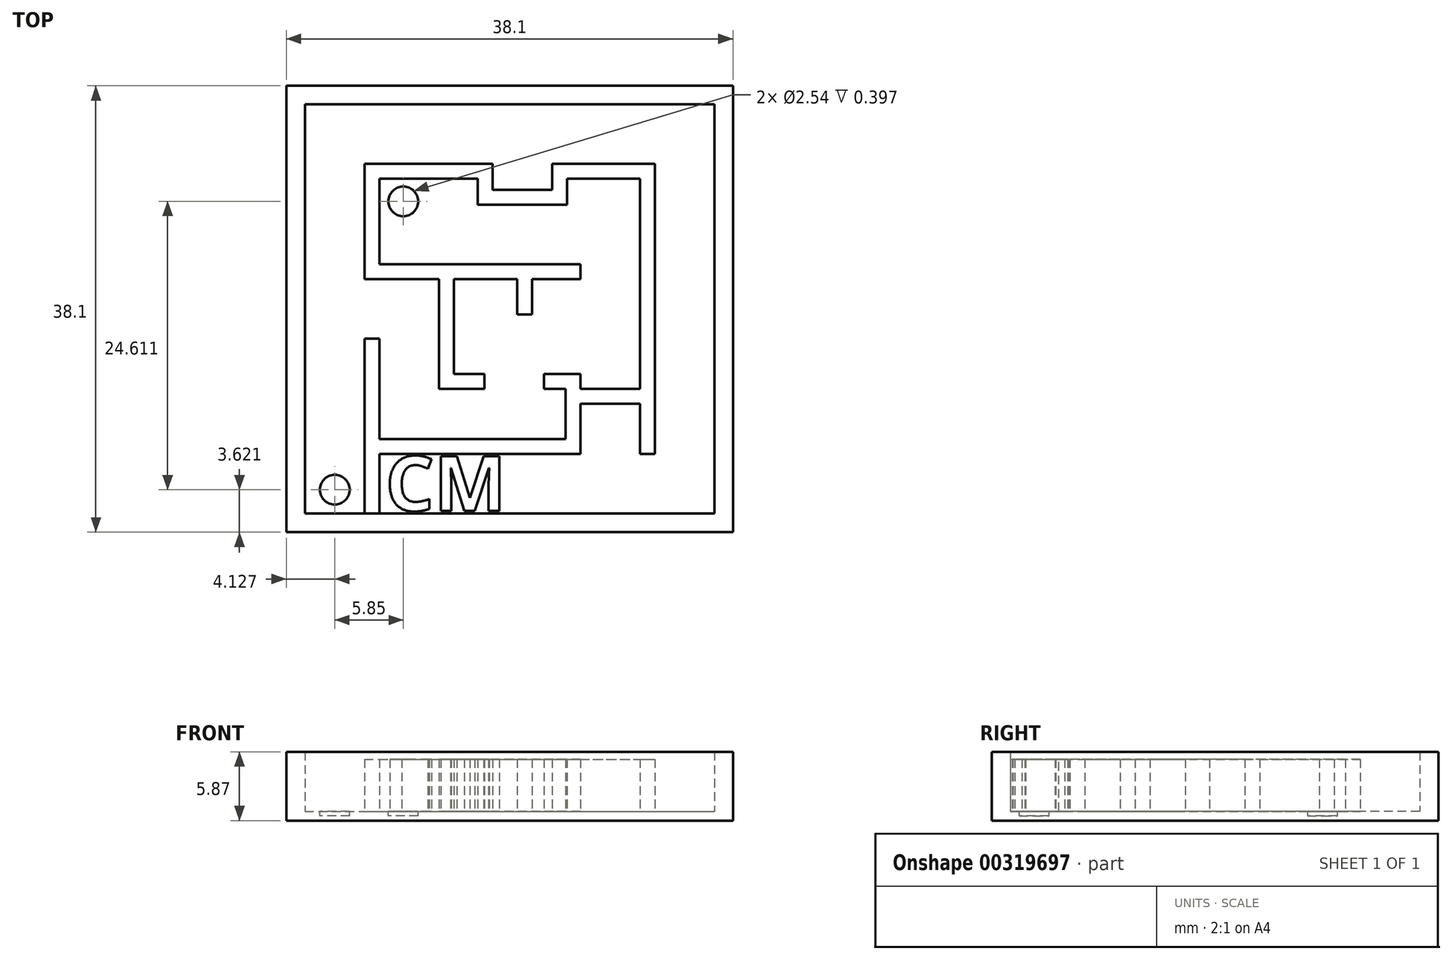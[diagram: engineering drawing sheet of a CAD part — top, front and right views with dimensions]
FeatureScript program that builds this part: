
annotation { "Feature Type Name" : "Feature", "Feature Type Description" : "" }
export const myFeature = defineFeature(function(context is Context, id is Id, definition is map)
    precondition{}
    {
        {
            var Q0;
            Q0=qCreatedBy(makeId("Top.planeOp"),FACE);
            var sketch = newSketch(context, id + "F0", { "sketchPlane" : qUnion([Q0])});
            skLineSegment(sketch, "E0.bottom", {"start": v(-16.34, 17.08) * mm, "end": v(21.76, 17.08) * mm});
            skLineSegment(sketch, "E0.top", {"start": v(-16.34, -21.02) * mm, "end": v(21.76, -21.02) * mm});
            skLineSegment(sketch, "E0.left", {"start": v(-16.34, 17.08) * mm, "end": v(-16.34, -21.02) * mm});
            skLineSegment(sketch, "E0.right", {"start": v(21.76, 17.08) * mm, "end": v(21.76, -21.02) * mm});
            skSolve(sketch);
        }
        {
            var Q0;
            Q0=makeQuery(id+"F0.imprint","IMPRINT",FACE,{"disambiguationData":[TD([[makeQuery(id+"F0.imprint","IMPRINT",EDGE,{"derivedFrom":sQuery(id+"F0.wireOp",EDGE,"E0.bottom")}),-1.0]])]});
            extrude(context, id + "F1", {"entities" : qUnion([Q0]), "depth" : 0.8 * mm});
        }
        {
            var Q0;
            Q0=makeQuery(id+"F1.opExtrude","CAP_FACE",FACE,{"disambiguationData":[OSD([sQuery(id+"F0.wireOp",EDGE,"E0.bottom"),sQuery(id+"F0.wireOp",EDGE,"E0.top"),sQuery(id+"F0.wireOp",EDGE,"E0.left"),sQuery(id+"F0.wireOp",EDGE,"E0.right")])],"isStart":false});
            var sketch = newSketch(context, id + "F2", { "sketchPlane" : qUnion([Q0])});
            skLineSegment(sketch, "E1.0", {"start": v(-14.75, 15.5) * mm, "end": v(20.17, 15.5) * mm});
            skLineSegment(sketch, "E1.1", {"start": v(-14.75, 15.5) * mm, "end": v(-14.75, -19.43) * mm});
            skLineSegment(sketch, "E1.2", {"start": v(-14.75, -19.43) * mm, "end": v(20.17, -19.43) * mm});
            skLineSegment(sketch, "E1.3", {"start": v(20.17, 15.5) * mm, "end": v(20.17, -19.43) * mm});
            skSolve(sketch);
        }
        {
            var Q0;
            Q0=makeQuery(id+"F2.imprint","IMPRINT",FACE,{"disambiguationData":[TD([[makeQuery(id+"F2.imprint","IMPRINT",EDGE,{"derivedFrom":sQuery(id+"F2.wireOp",EDGE,"E1.0")}),1.0]])]});
            extrude(context, id + "F3", {"entities" : qUnion([Q0]), "operationType" : NewBodyOperationType.ADD, "depth" : 5.08 * mm});
        }
        {
            var Q0;
            Q0=makeQuery(id+"F1.opExtrude","CAP_FACE",FACE,{"disambiguationData":[OSD([sQuery(id+"F0.wireOp",EDGE,"E0.bottom"),sQuery(id+"F0.wireOp",EDGE,"E0.top"),sQuery(id+"F0.wireOp",EDGE,"E0.left"),sQuery(id+"F0.wireOp",EDGE,"E0.right")])],"isStart":false});
            var sketch = newSketch(context, id + "F4", { "sketchPlane" : qUnion([Q0])});
            skLineSegment(sketch, "E2.bottom", {"start": v(-9.67, -19.43) * mm, "end": v(-8.4, -19.43) * mm});
            skLineSegment(sketch, "E2.top", {"start": v(-9.67, 10.41) * mm, "end": v(-8.4, 10.41) * mm});
            skLineSegment(sketch, "E2.left", {"start": v(-9.67, -19.43) * mm, "end": v(-9.67, -4.5) * mm});
            skLineSegment(sketch, "E2.right", {"start": v(-8.4, -19.43) * mm, "end": v(-8.4, -4.5) * mm});
            skLineSegment(sketch, "E3", {"start": v(-9.67, 0.57) * mm, "end": v(-8.4, 0.57) * mm});
            skLineSegment(sketch, "E4", {"start": v(-9.67, -4.5) * mm, "end": v(-8.4, -4.5) * mm});
            skLineSegment(sketch, "E5.trimOffspring", {"start": v(-9.67, 0.57) * mm, "end": v(-9.67, 10.41) * mm});
            skLineSegment(sketch, "E6.trimOffspring", {"start": v(-8.4, 0.57) * mm, "end": v(-8.4, 10.41) * mm});
            skLineSegment(sketch, "E7.bottom", {"start": v(-8.4, 10.41) * mm, "end": v(1.27, 10.41) * mm});
            skLineSegment(sketch, "E7.top", {"start": v(-8.4, 9.14) * mm, "end": v(1.27, 9.14) * mm});
            skLineSegment(sketch, "E7.left", {"start": v(-8.4, 10.41) * mm, "end": v(-8.4, 9.14) * mm});
            skLineSegment(sketch, "E7.right", {"start": v(15.1, 10.41) * mm, "end": v(15.1, 9.14) * mm});
            skLineSegment(sketch, "E8.bottom", {"start": v(15.1, 9.14) * mm, "end": v(13.82, 9.14) * mm});
            skLineSegment(sketch, "E8.top", {"start": v(15.1, 4.7) * mm, "end": v(13.82, 4.7) * mm});
            skLineSegment(sketch, "E8.left", {"start": v(15.1, 9.14) * mm, "end": v(15.1, 4.7) * mm});
            skLineSegment(sketch, "E8.right", {"start": v(13.82, 9.14) * mm, "end": v(13.82, 4.7) * mm});
            skLineSegment(sketch, "E9.bottom", {"start": v(-8.4, 0.57) * mm, "end": v(-2.05, 0.57) * mm});
            skLineSegment(sketch, "E9.top", {"start": v(-8.4, 1.84) * mm, "end": v(-2.05, 1.84) * mm});
            skLineSegment(sketch, "E9.left", {"start": v(-8.4, 0.57) * mm, "end": v(-8.4, 1.84) * mm});
            skLineSegment(sketch, "E9.right", {"start": v(-2.05, 0.57) * mm, "end": v(-2.05, 1.84) * mm});
            skLineSegment(sketch, "E10.bottom", {"start": v(-2.05, 0.57) * mm, "end": v(-3.32, 0.57) * mm});
            skLineSegment(sketch, "E10.top", {"start": v(-2.05, -8) * mm, "end": v(-3.32, -8) * mm});
            skLineSegment(sketch, "E10.left", {"start": v(-2.05, 0.57) * mm, "end": v(-2.05, -8) * mm});
            skLineSegment(sketch, "E10.right", {"start": v(-3.32, 0.57) * mm, "end": v(-3.32, -8) * mm});
            skPoint(sketch, "E11.oppositeSnap0", {"position": v(13.82, 6.92) * mm});
            skLineSegment(sketch, "E11.bottom", {"start": v(-3.32, 9.14) * mm, "end": v(-2.05, 9.14) * mm});
            skLineSegment(sketch, "E12.bottom", {"start": v(13.82, 4.7) * mm, "end": v(15.1, 4.7) * mm});
            skLineSegment(sketch, "E12.top", {"start": v(13.82, -8) * mm, "end": v(15.1, -8) * mm});
            skLineSegment(sketch, "E12.left", {"start": v(13.82, 4.7) * mm, "end": v(13.82, -8) * mm});
            skLineSegment(sketch, "E12.right", {"start": v(15.1, 4.7) * mm, "end": v(15.1, -8) * mm});
            skLineSegment(sketch, "E13.bottom", {"start": v(-2.05, 0.57) * mm, "end": v(8.74, 0.57) * mm});
            skLineSegment(sketch, "E13.top", {"start": v(-2.05, 1.84) * mm, "end": v(8.74, 1.84) * mm});
            skLineSegment(sketch, "E13.right", {"start": v(8.74, 0.57) * mm, "end": v(8.74, 1.84) * mm});
            skLineSegment(sketch, "E14.bottom", {"start": v(-0.71, 1.84) * mm, "end": v(0.56, 1.84) * mm});
            skLineSegment(sketch, "E15.bottom", {"start": v(11.44, 9.14) * mm, "end": v(10.17, 9.14) * mm});
            skLineSegment(sketch, "E16.bottom", {"start": v(-8.4, -13.08) * mm, "end": v(8.74, -13.08) * mm});
            skLineSegment(sketch, "E16.top", {"start": v(-8.4, -14.35) * mm, "end": v(8.74, -14.35) * mm});
            skLineSegment(sketch, "E16.left", {"start": v(-8.4, -13.08) * mm, "end": v(-8.4, -14.35) * mm});
            skLineSegment(sketch, "E16.right", {"start": v(8.74, -13.08) * mm, "end": v(8.74, -14.35) * mm});
            skLineSegment(sketch, "E17.top", {"start": v(13.82, -14.35) * mm, "end": v(15.1, -14.35) * mm});
            skLineSegment(sketch, "E17.left", {"start": v(13.82, -8) * mm, "end": v(13.82, -14.35) * mm});
            skLineSegment(sketch, "E17.right", {"start": v(15.1, -8) * mm, "end": v(15.1, -14.35) * mm});
            skLineSegment(sketch, "E18.bottom", {"start": v(8.74, -13.08) * mm, "end": v(7.47, -13.08) * mm});
            skLineSegment(sketch, "E18.top", {"start": v(8.74, -8.8) * mm, "end": v(7.47, -8.8) * mm});
            skLineSegment(sketch, "E18.left", {"start": v(8.74, -13.08) * mm, "end": v(8.74, -8.8) * mm});
            skLineSegment(sketch, "E18.right", {"start": v(7.47, -13.08) * mm, "end": v(7.47, -8.8) * mm});
            skPoint(sketch, "E19.oppositeSnap0", {"position": v(8.1, -8.8) * mm});
            skLineSegment(sketch, "E19.bottom", {"start": v(8.74, -10.06) * mm, "end": v(13.88, -10.06) * mm});
            skLineSegment(sketch, "E19.top", {"start": v(8.74, -8.8) * mm, "end": v(13.88, -8.8) * mm});
            skLineSegment(sketch, "E19.left", {"start": v(8.74, -10.06) * mm, "end": v(8.74, -8.8) * mm});
            skLineSegment(sketch, "E19.right", {"start": v(13.88, -10.06) * mm, "end": v(13.88, -8.8) * mm});
            skLineSegment(sketch, "E20.left", {"start": v(-2.05, -1.65) * mm, "end": v(-2.05, -1.65) * mm});
            skLineSegment(sketch, "E20.right", {"start": v(13.82, -1.65) * mm, "end": v(13.82, -1.65) * mm});
            skLineSegment(sketch, "E21.bottom", {"start": v(7.47, -8.8) * mm, "end": v(5.62, -8.8) * mm});
            skLineSegment(sketch, "E21.top", {"start": v(7.47, -7.52) * mm, "end": v(5.62, -7.52) * mm});
            skLineSegment(sketch, "E21.left", {"start": v(7.47, -7.52) * mm, "end": v(7.47, -8.8) * mm});
            skPoint(sketch, "E22.oppositeSnap0", {"position": v(2.52, -7.52) * mm});
            skLineSegment(sketch, "E22.top", {"start": v(-2.05, -7.52) * mm, "end": v(-3.32, -7.52) * mm});
            skLineSegment(sketch, "E22.left", {"start": v(-2.05, -7.52) * mm, "end": v(-2.05, -8) * mm});
            skLineSegment(sketch, "E22.right", {"start": v(-3.32, -7.52) * mm, "end": v(-3.32, -8) * mm});
            skLineSegment(sketch, "E23", {"start": v(0.54, -8.8) * mm, "end": v(0.54, -7.52) * mm});
            skLineSegment(sketch, "E24", {"start": v(5.62, -8.8) * mm, "end": v(5.62, -7.52) * mm});
            skLineSegment(sketch, "E25.trimOffspring", {"start": v(0.54, -8.8) * mm, "end": v(-2.43, -8.8) * mm});
            skLineSegment(sketch, "E26.trimOffspring", {"start": v(0.54, -7.52) * mm, "end": v(-2.43, -7.52) * mm});
            skLineSegment(sketch, "E27.left", {"start": v(-2.05, -3.71) * mm, "end": v(-2.05, -2.07) * mm});
            skLineSegment(sketch, "E27.right", {"start": v(13.82, -3.71) * mm, "end": v(13.82, -2.07) * mm});
            skLineSegment(sketch, "E28.bottom", {"start": v(7.47, -7.52) * mm, "end": v(8.74, -7.52) * mm});
            skLineSegment(sketch, "E28.top", {"start": v(7.47, -8.8) * mm, "end": v(8.74, -8.8) * mm});
            skLineSegment(sketch, "E28.right", {"start": v(8.74, -7.52) * mm, "end": v(8.74, -8.8) * mm});
            skLineSegment(sketch, "E29", {"start": v(-2.43, -8.8) * mm, "end": v(-3.32, -8.8) * mm});
            skLineSegment(sketch, "E30", {"start": v(-3.32, -8.8) * mm, "end": v(-3.32, -8) * mm});
            skLineSegment(sketch, "E31", {"start": v(1.27, 10.41) * mm, "end": v(1.27, 9.14) * mm});
            skLineSegment(sketch, "E32", {"start": v(6.35, 10.41) * mm, "end": v(6.35, 9.14) * mm});
            skLineSegment(sketch, "E33.trimOffspring", {"start": v(6.35, 10.41) * mm, "end": v(15.1, 10.41) * mm});
            skLineSegment(sketch, "E34.trimOffspring", {"start": v(6.35, 9.14) * mm, "end": v(10.17, 9.14) * mm});
            skLineSegment(sketch, "E35.trimOffspring", {"start": v(11.44, 9.14) * mm, "end": v(15.1, 9.14) * mm});
            skPoint(sketch, "E36.right.end.orphan", {"position": v(5.88, -2.07) * mm});
            skPoint(sketch, "E11.top.end.orphan", {"position": v(-3.32, 6.92) * mm});
            skLineSegment(sketch, "E37.bottom", {"start": v(1.27, 9.14) * mm, "end": v(0, 9.14) * mm});
            skLineSegment(sketch, "E37.top", {"start": v(1.27, 6.92) * mm, "end": v(0, 6.92) * mm});
            skLineSegment(sketch, "E37.left", {"start": v(1.27, 9.14) * mm, "end": v(1.27, 6.92) * mm});
            skLineSegment(sketch, "E37.right", {"start": v(0, 9.14) * mm, "end": v(0, 6.92) * mm});
            skLineSegment(sketch, "E38.bottom", {"start": v(1.27, 6.92) * mm, "end": v(6.35, 6.92) * mm});
            skLineSegment(sketch, "E38.top", {"start": v(1.27, 8.2) * mm, "end": v(6.35, 8.2) * mm});
            skLineSegment(sketch, "E38.left", {"start": v(1.27, 6.92) * mm, "end": v(1.27, 8.2) * mm});
            skLineSegment(sketch, "E38.right", {"start": v(6.35, 6.92) * mm, "end": v(6.35, 8.2) * mm});
            skLineSegment(sketch, "E39.bottom", {"start": v(6.35, 8.2) * mm, "end": v(7.62, 8.2) * mm});
            skLineSegment(sketch, "E39.top", {"start": v(6.35, 9.14) * mm, "end": v(7.62, 9.14) * mm});
            skLineSegment(sketch, "E39.left", {"start": v(6.35, 8.2) * mm, "end": v(6.35, 9.14) * mm});
            skLineSegment(sketch, "E39.right", {"start": v(7.62, 8.2) * mm, "end": v(7.62, 9.14) * mm});
            skLineSegment(sketch, "E40.bottom", {"start": v(7.62, 8.2) * mm, "end": v(6.35, 8.2) * mm});
            skLineSegment(sketch, "E40.top", {"start": v(7.62, 6.92) * mm, "end": v(6.35, 6.92) * mm});
            skLineSegment(sketch, "E40.left", {"start": v(7.62, 8.2) * mm, "end": v(7.62, 6.92) * mm});
            skLineSegment(sketch, "E40.right", {"start": v(6.35, 8.2) * mm, "end": v(6.35, 6.92) * mm});
            skLineSegment(sketch, "E41.bottom", {"start": v(3.34, 0.57) * mm, "end": v(4.61, 0.57) * mm});
            skLineSegment(sketch, "E41.top", {"start": v(3.34, -2.44) * mm, "end": v(4.61, -2.44) * mm});
            skLineSegment(sketch, "E41.left", {"start": v(3.34, 0.57) * mm, "end": v(3.34, -2.44) * mm});
            skLineSegment(sketch, "E41.right", {"start": v(4.61, 0.57) * mm, "end": v(4.61, -2.44) * mm});
            skText(sketch, "E42", { "text": "CM\n", "fontName": "OpenSans-Bold.ttf"});
            const initialGuessF4  = {"E42": [-0.00789, -0.0192, 1, 0, 0.0047]};
            skSetInitialGuess(sketch, initialGuessF4);
            skSolve(sketch);
        }
        {
            var Q0;
            Q0 = qSketchRegion(id + "F4", true);
            var Q1;
            Q1=makeQuery(id+"F4.imprint","IMPRINT",FACE,{"disambiguationData":[TD([[makeQuery(id+"F4.imprint","IMPRINT",EDGE,{"derivedFrom":sQuery(id+"F4.wireOp",EDGE,"E9.bottom")}),1.0]])]});
            var Q2;
            Q2=makeQuery(id+"F4.imprint","IMPRINT",FACE,{"disambiguationData":[TD([[makeQuery(id+"F4.imprint","IMPRINT",EDGE,{"derivedFrom":sQuery(id+"F4.wireOp",EDGE,"E18.bottom")}),-1.0]])]});
            var Q3;
            Q3=makeQuery(id+"F4.imprint","IMPRINT",FACE,{"disambiguationData":[TD([[makeQuery(id+"F4.imprint","IMPRINT",EDGE,{"derivedFrom":sQuery(id+"F4.wireOp",EDGE,"E38.bottom")}),1.0]])]});
            var Q4;
            Q4=makeQuery(id+"F4.imprint","IMPRINT",FACE,{"disambiguationData":[TD([[makeQuery(id+"F4.imprint","IMPRINT",EDGE,{"derivedFrom":sQuery(id+"F4.wireOp",EDGE,"E37.bottom")}),1.0]])]});
            var Q5;
            Q5=makeQuery(id+"F4.imprint","IMPRINT",FACE,{"disambiguationData":[TD([[makeQuery(id+"F4.imprint","IMPRINT",EDGE,{"derivedFrom":sQuery(id+"F4.wireOp",EDGE,"E21.bottom")}),-1.0]])]});
            var Q6;
            {var subQ3=sQuery(id+"F4.wireOp",EDGE,"E9.right");Q6=makeQuery(id+"F4.imprint","IMPRINT",FACE,{"disambiguationData":[TD([[makeQuery(id+"F4.imprint","IMPRINT",EDGE,{"derivedFrom":subQ3}),-1.0]])]});}
            var Q7;
            Q7=makeQuery(id+"F4.imprint","IMPRINT",FACE,{"disambiguationData":[TD([[makeQuery(id+"F4.imprint","IMPRINT",EDGE,{"derivedFrom":sQuery(id+"F4.wireOp",EDGE,"E16.bottom")}),-1.0]])]});
            var Q8;
            {var subQ5=sQuery(id+"F4.wireOp",EDGE,"E19.left");Q8=makeQuery(id+"F4.imprint","IMPRINT",FACE,{"disambiguationData":[TD([[makeQuery(id+"F4.imprint","IMPRINT",EDGE,{"derivedFrom":subQ5}),-1.0]])]});}
            var Q9;
            Q9=makeQuery(id+"F4.imprint","IMPRINT",FACE,{"disambiguationData":[TD([[makeQuery(id+"F4.imprint","IMPRINT",EDGE,{"derivedFrom":sQuery(id+"F4.wireOp",EDGE,"E40.bottom")}),1.0]])]});
            var Q10;
            Q10=makeQuery(id+"F4.imprint","IMPRINT",FACE,{"disambiguationData":[TD([[makeQuery(id+"F4.imprint","IMPRINT",EDGE,{"derivedFrom":sQuery(id+"F4.wireOp",EDGE,"E39.top")}),-1.0]])]});
            var Q11;
            {var subQ3=sQuery(id+"F4.wireOp",EDGE,"E22.top");Q11=makeQuery(id+"F4.imprint","IMPRINT",FACE,{"disambiguationData":[TD([[makeQuery(id+"F4.imprint","IMPRINT",EDGE,{"derivedFrom":subQ3}),1.0]])]});}
            var Q12;
            Q12=makeQuery(id+"F4.imprint","IMPRINT",FACE,{"disambiguationData":[TD([[makeQuery(id+"F4.imprint","IMPRINT",EDGE,{"derivedFrom":sQuery(id+"F4.wireOp",EDGE,"E41.bottom")}),-1.0]])]});
            var Q13;
            {var subQ4=sQuery(id+"F4.wireOp",EDGE,"E10.bottom");Q13=makeQuery(id+"F4.imprint","IMPRINT",FACE,{"disambiguationData":[TD([[makeQuery(id+"F4.imprint","IMPRINT",EDGE,{"derivedFrom":subQ4}),1.0]])]});}
            var Q14;
            Q14=makeQuery(id+"F4.imprint","IMPRINT",FACE,{"disambiguationData":[TD([[makeQuery(id+"F4.imprint","IMPRINT",EDGE,{"derivedFrom":sQuery(id+"F4.wireOp",EDGE,"E28.bottom")}),-1.0]])]});
            var Q15;
            {var subQ5=sQuery(id+"F4.wireOp",EDGE,"E19.right");Q15=makeQuery(id+"F4.imprint","IMPRINT",FACE,{"disambiguationData":[TD([[makeQuery(id+"F4.imprint","IMPRINT",EDGE,{"derivedFrom":subQ5}),1.0]])]});}
            extrude(context, id + "F5", {"entities" : qUnion([Q0, Q1, Q2, Q3, Q4, Q5, Q6, Q7, Q8, Q9, Q10, Q11, Q12, Q13, Q14, Q15]), "operationType" : NewBodyOperationType.ADD, "depth" : 4.44 * mm});
        }
        {
            var Q0;
            Q0=makeQuery(id+"F1.opExtrude","CAP_FACE",FACE,{"disambiguationData":[OSD([sQuery(id+"F0.wireOp",EDGE,"E0.bottom"),sQuery(id+"F0.wireOp",EDGE,"E0.top"),sQuery(id+"F0.wireOp",EDGE,"E0.left"),sQuery(id+"F0.wireOp",EDGE,"E0.right")])],"isStart":false});
            var sketch = newSketch(context, id + "F6", { "sketchPlane" : qUnion([Q0])});
            skCircle(sketch, "E43", {"center": v(-12.21, -17.4) * mm, "radius": 1.27 * mm});
            skPoint(sketch, "E43.centerSnap0", {"position": v(-12.21, -19.43) * mm});
            skCircle(sketch, "E44", {"center": v(-6.36, 7.21) * mm, "radius": 1.27 * mm});
            skSolve(sketch);
        }
        {
            var Q0;
            Q0=makeQuery(id+"F6.imprint","IMPRINT",FACE,{"disambiguationData":[TD([[makeQuery(id+"F6.imprint","IMPRINT",EDGE,{"derivedFrom":sQuery(id+"F6.wireOp",EDGE,"E44")}),1.0]])]});
            var Q1;
            Q1=makeQuery(id+"F6.imprint","IMPRINT",FACE,{"disambiguationData":[TD([[makeQuery(id+"F6.imprint","IMPRINT",EDGE,{"derivedFrom":sQuery(id+"F6.wireOp",EDGE,"E43")}),1.0]])]});
            extrude(context, id + "F7", {"entities" : qUnion([Q0, Q1]), "operationType" : NewBodyOperationType.REMOVE, "oppositeDirection" : true, "depth" : 0.4 * mm});
        }
    });
